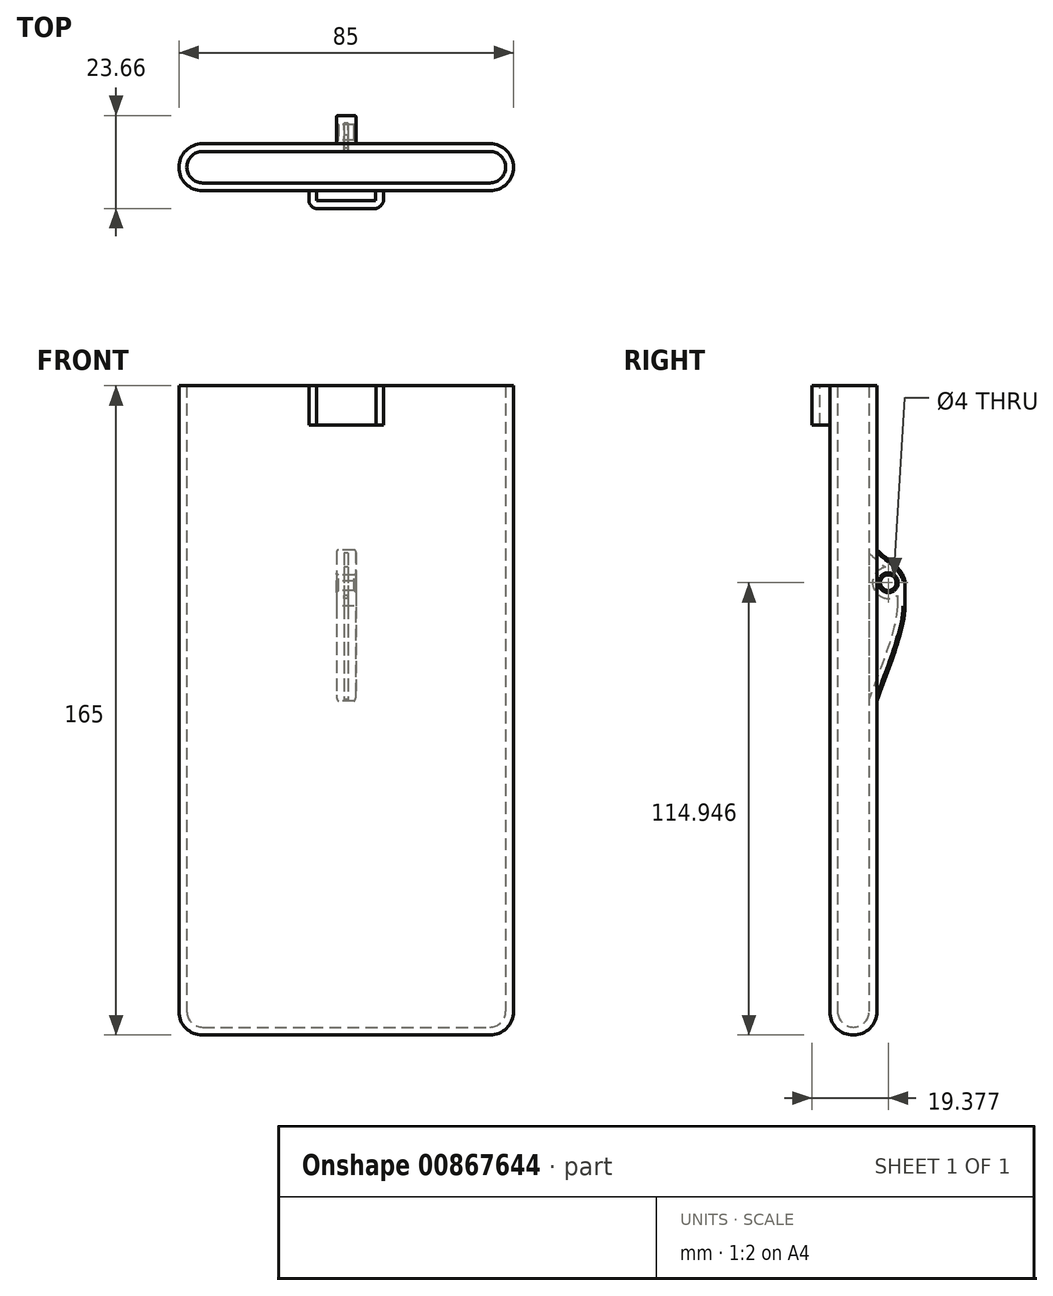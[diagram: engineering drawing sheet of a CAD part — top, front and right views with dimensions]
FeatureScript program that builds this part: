
annotation { "Feature Type Name" : "Feature", "Feature Type Description" : "" }
export const myFeature = defineFeature(function(context is Context, id is Id, definition is map)
    precondition{}
    {
        {
            var Q0;
            Q0=qCreatedBy(makeId("Front.planeOp"),FACE);
            var sketch = newSketch(context, id + "F0", { "sketchPlane" : qUnion([Q0])});
            skLineSegment(sketch, "E0.bottom", {"start": v(42.5, 82.5) * mm, "end": v(-42.5, 82.5) * mm});
            skLineSegment(sketch, "E0.top", {"start": v(36.5, -82.5) * mm, "end": v(-36.5, -82.5) * mm});
            skLineSegment(sketch, "E0.left", {"start": v(42.5, 82.5) * mm, "end": v(42.5, -76.5) * mm});
            skLineSegment(sketch, "E0.right", {"start": v(-42.5, 82.5) * mm, "end": v(-42.5, -76.5) * mm});
            skPoint(sketch, "E0.middle", {"position": v(0, 0) * mm});
            skPoint(sketch, "E1.orphan", {"position": v(-42.5, -82.5) * mm});
            skPoint(sketch, "E2.orphan", {"position": v(42.5, -82.5) * mm});
            skLineSegment(sketch, "E3", {"start": v(36.5, -82.5) * mm, "end": v(36.5, 82.5) * mm});
            skLineSegment(sketch, "E4", {"start": v(42.5, -76.5) * mm, "end": v(-42.5, -76.5) * mm});
            skLineSegment(sketch, "E5", {"start": v(-36.5, -82.5) * mm, "end": v(-36.5, 82.5) * mm});
            skArc(sketch, "E6", {"start": v(36.5, -82.5) * mm, "mid": v(40.74, -80.74) * mm, "end": v(42.5, -76.5) * mm});
            skArc(sketch, "E7", {"start": v(-42.5, -76.5) * mm, "mid": v(-40.74, -80.74) * mm, "end": v(-36.5, -82.5) * mm});
            skSolve(sketch);
        }
        {
            var Q0;
            Q0=qCreatedBy(makeId("Right.planeOp"),FACE);
            var sketch = newSketch(context, id + "F1", { "sketchPlane" : qUnion([Q0])});
            skLineSegment(sketch, "E8", {"start": v(20.64, 40.42) * mm, "end": v(20.69, 40.42) * mm});
            skLineSegment(sketch, "E9", {"start": v(13.16, 32.9) * mm, "end": v(13.16, 26.53) * mm});
            skFitSpline(sketch, "E10", {"points": [v(13.16, 26.53) * mm, v(5.97, 2.35) * mm], "startDerivative": vector(0.3, -17.47) * mm, "endDerivative": vector(-6.38, -18.09) * mm});
            skPoint(sketch, "E11.centerSnap0", {"position": v(16.3, 40.42) * mm});
            skArc(sketch, "E12", {"start": v(13.16, 32) * mm, "mid": v(13.2, 32.45) * mm, "end": v(13.16, 32.9) * mm});
            skPoint(sketch, "E13.orphan", {"position": v(13.16, 40.42) * mm});
            skLineSegment(sketch, "E14", {"start": v(6, 2.42) * mm, "end": v(5.97, 2.35) * mm});
            skFitSpline(sketch, "E15", {"points": [v(6, 40.79) * mm, v(13.16, 32.9) * mm], "startDerivative": vector(7.97, -7.88) * mm, "endDerivative": vector(2.73, -10.61) * mm});
            skPoint(sketch, "E16.end.orphan", {"position": v(19.43, 40.42) * mm});
            skLineSegment(sketch, "E17", {"start": v(6, 40.79) * mm, "end": v(6, 2.42) * mm});
            skCircle(sketch, "E18", {"center": v(8.88, 32.45) * mm, "radius": 2 * mm});
            skSolve(sketch);
        }
        {
            var Q0;
            {var subQ0=sQuery(id+"F0.wireOp",EDGE,"E3");var subQ1=sQuery(id+"F0.wireOp",EDGE,"E0.bottom");var subQ2=makeQuery(id+"F0.imprint","INTERSECT",VERTEX,{"derivedFrom":[subQ1,subQ0]});Q0=makeQuery(id+"F0.imprint","IMPRINT",FACE,{"disambiguationData":[TD([[makeQuery(id+"F0.imprint","IMPRINT",EDGE,{"disambiguationData":[TD([[subQ2,-1.0]])],"derivedFrom":subQ1}),1.0]])]});}
            extrude(context, id + "F2", {"entities" : qUnion([Q0]), "endBound" : BoundingType.SYMMETRIC, "depth" : 12 * mm, "offsetDistance" : 25 * mm});
        }
        {
            var Q0;
            {var subQ0=sQuery(id+"F0.wireOp",EDGE,"E0.right");Q0=makeQuery(id+"F0.imprint","IMPRINT",FACE,{"disambiguationData":[TD([[makeQuery(id+"F0.imprint","IMPRINT",EDGE,{"derivedFrom":subQ0}),1.0]])]});}
            var Q1;
            Q1=sQuery(id+"F0.wireOp",EDGE,"E5");
            revolve(context, id + "F3", {"operationType" : NewBodyOperationType.ADD, "surfaceOperationType" : NewSurfaceOperationType.NEW, "entities" : qUnion([Q0]), "axis" : qUnion([Q1]), "revolveType" : RevolveType.FULL});
        }
        {
            var Q0;
            {var subQ0=sQuery(id+"F0.wireOp",EDGE,"E0.left");Q0=makeQuery(id+"F0.imprint","IMPRINT",FACE,{"disambiguationData":[TD([[makeQuery(id+"F0.imprint","IMPRINT",EDGE,{"derivedFrom":subQ0}),-1.0]])]});}
            var Q1;
            Q1=sQuery(id+"F0.wireOp",EDGE,"E3");
            revolve(context, id + "F4", {"operationType" : NewBodyOperationType.ADD, "surfaceOperationType" : NewSurfaceOperationType.NEW, "entities" : qUnion([Q0]), "axis" : qUnion([Q1]), "revolveType" : RevolveType.FULL});
        }
        {
            var Q0;
            {var subQ0=sQuery(id+"F0.wireOp",EDGE,"E0.top");Q0=makeQuery(id+"F0.imprint","IMPRINT",FACE,{"disambiguationData":[TD([[makeQuery(id+"F0.imprint","IMPRINT",EDGE,{"derivedFrom":subQ0}),-1.0]])]});}
            var Q1;
            Q1=sQuery(id+"F0.wireOp",EDGE,"E4");
            revolve(context, id + "F5", {"operationType" : NewBodyOperationType.ADD, "surfaceOperationType" : NewSurfaceOperationType.NEW, "entities" : qUnion([Q0]), "axis" : qUnion([Q1]), "revolveType" : RevolveType.FULL});
        }
        {
            var Q0;
            {var subQ0=sQuery(id+"F0.wireOp",EDGE,"E6");Q0=makeQuery(id+"F0.imprint","IMPRINT",FACE,{"disambiguationData":[TD([[makeQuery(id+"F0.imprint","IMPRINT",EDGE,{"derivedFrom":subQ0}),1.0]])]});}
            var Q1;
            Q1=sQuery(id+"F0.wireOp",EDGE,"E4");
            revolve(context, id + "F6", {"operationType" : NewBodyOperationType.ADD, "surfaceOperationType" : NewSurfaceOperationType.NEW, "entities" : qUnion([Q0]), "axis" : qUnion([Q1]), "revolveType" : RevolveType.FULL});
        }
        {
            var Q0;
            {var subQ0=sQuery(id+"F0.wireOp",EDGE,"E7");Q0=makeQuery(id+"F0.imprint","IMPRINT",FACE,{"disambiguationData":[TD([[makeQuery(id+"F0.imprint","IMPRINT",EDGE,{"derivedFrom":subQ0}),1.0]])]});}
            var Q1;
            Q1=sQuery(id+"F0.wireOp",EDGE,"E4");
            revolve(context, id + "F7", {"operationType" : NewBodyOperationType.ADD, "surfaceOperationType" : NewSurfaceOperationType.NEW, "entities" : qUnion([Q0]), "axis" : qUnion([Q1]), "revolveType" : RevolveType.FULL});
        }
        {
            var Q0;
            {var subQ0=sQuery(id+"F1.wireOp",EDGE,"E10");Q0=makeQuery(id+"F1.imprint","IMPRINT",FACE,{"disambiguationData":[TD([[makeQuery(id+"F1.imprint","IMPRINT",EDGE,{"derivedFrom":subQ0}),-1.0]])]});}
            extrude(context, id + "F8", {"entities" : qUnion([Q0]), "operationType" : NewBodyOperationType.ADD, "endBound" : BoundingType.SYMMETRIC, "depth" : 5 * mm, "offsetDistance" : 25 * mm});
        }
        {
            var Q0;
            {var subQ0=sQuery(id+"F0.wireOp",EDGE,"E0.bottom");Q0=makeQuery(id+"F4.boolean.opBoolean","MERGE",FACE,{"derivedFrom":[makeQuery(id+"F3.boolean.opBoolean","MERGE",FACE,{"derivedFrom":[makeQuery(id+"F2.opExtrude","SWEPT_FACE",FACE,{"disambiguationData":[OSD([subQ0])]}),makeQuery(id+"F3.opRevolve","SWEPT_FACE",FACE,{"disambiguationData":[OSD([subQ0])]})]}),makeQuery(id+"F4.opRevolve","SWEPT_FACE",FACE,{"disambiguationData":[OSD([subQ0])]})]});}
            shell(context, id + "F9", {"entities" : qUnion([Q0]), "thickness" : 2 * mm});
        }
        {
            var Q0;
            Q0=makeQuery(id+"F8.opExtrude","CAP_EDGE",EDGE,{"disambiguationData":[OSD([sQuery(id+"F1.wireOp",EDGE,"E15")])],"isStart":false});
            var Q1;
            Q1=makeQuery(id+"F8.opExtrude","CAP_EDGE",EDGE,{"disambiguationData":[OSD([sQuery(id+"F1.wireOp",EDGE,"E9")])],"isStart":false});
            var Q2;
            Q2=makeQuery(id+"F8.opExtrude","CAP_EDGE",EDGE,{"disambiguationData":[OSD([sQuery(id+"F1.wireOp",EDGE,"E10")])],"isStart":false});
            var Q3;
            Q3=makeQuery(id+"F8.opExtrude","CAP_EDGE",EDGE,{"disambiguationData":[OSD([sQuery(id+"F1.wireOp",EDGE,"E10")])],"isStart":true});
            var Q4;
            Q4=makeQuery(id+"F8.opExtrude","CAP_EDGE",EDGE,{"disambiguationData":[OSD([sQuery(id+"F1.wireOp",EDGE,"E9")])],"isStart":true});
            var Q5;
            Q5=makeQuery(id+"F8.opExtrude","CAP_EDGE",EDGE,{"disambiguationData":[OSD([sQuery(id+"F1.wireOp",EDGE,"E15")])],"isStart":true});
            fillet(context, id + "F10", {"entities" : qUnion([Q0, Q1, Q2, Q3, Q4, Q5]), "radius" : 0.5 * mm, "tangentPropagation" : true, "allowEdgeOverflow" : false});
        }
        {
            var Q0;
            Q0=makeQuery(id+"F8.opExtrude","CAP_EDGE",EDGE,{"disambiguationData":[OSD([sQuery(id+"F1.wireOp",EDGE,"E18")])],"isStart":false});
            var Q1;
            Q1=makeQuery(id+"F8.opExtrude","CAP_EDGE",EDGE,{"disambiguationData":[OSD([sQuery(id+"F1.wireOp",EDGE,"E18")])],"isStart":true});
            chamfer(context, id + "F11", {"entities" : qUnion([Q0, Q1]), "width" : 0.5 * mm, "tangentPropagation" : true});
        }
        {
            var Q0;
            {var subQ0=sQuery(id+"F0.wireOp",EDGE,"E0.bottom");Q0=makeQuery(id+"F4.boolean.opBoolean","MERGE",FACE,{"derivedFrom":[makeQuery(id+"F3.boolean.opBoolean","MERGE",FACE,{"derivedFrom":[makeQuery(id+"F2.opExtrude","SWEPT_FACE",FACE,{"disambiguationData":[OSD([subQ0])]}),makeQuery(id+"F3.opRevolve","SWEPT_FACE",FACE,{"disambiguationData":[OSD([subQ0])]})]}),makeQuery(id+"F4.opRevolve","SWEPT_FACE",FACE,{"disambiguationData":[OSD([subQ0])]})]});}
            var sketch = newSketch(context, id + "F12", { "sketchPlane" : qUnion([Q0])});
            skSolve(sketch);
        }
        {
            var Q0;
            {var subQ1=sQuery(id+"F0.wireOp",EDGE,"E0.bottom");var subQ4=makeQuery(id+"F2.opExtrude","CAP_EDGE",EDGE,{"disambiguationData":[OSD([subQ1])],"isStart":true});Q0=makeQuery(id+"F12.imprint","IMPRINT",FACE,{"disambiguationData":[TD([[makeQuery(id+"F12.imprint","IMPRINT",EDGE,{"derivedFrom":subQ4}),1.0]])]});}
            var sketch = newSketch(context, id + "F13", { "sketchPlane" : qUnion([Q0])});
            skLineSegment(sketch, "E19.bottom", {"start": v(7.5, -8.5) * mm, "end": v(-7.5, -8.5) * mm});
            skLineSegment(sketch, "E19.top", {"start": v(7.5, -6) * mm, "end": v(-7.5, -6) * mm});
            skLineSegment(sketch, "E19.left", {"start": v(7.5, -8.5) * mm, "end": v(7.5, -6) * mm});
            skLineSegment(sketch, "E19.right", {"start": v(-7.5, -8.5) * mm, "end": v(-7.5, -6) * mm});
            skPoint(sketch, "E19.middle", {"position": v(0, -7.25) * mm});
            skLineSegment(sketch, "E20.0", {"start": v(7.52, -10.5) * mm, "end": v(-7.5, -10.5) * mm});
            skLineSegment(sketch, "E21.0", {"start": v(9.5, -8.5) * mm, "end": v(9.5, -6) * mm});
            skLineSegment(sketch, "E22.0", {"start": v(-9.5, -8.5) * mm, "end": v(-9.5, -6) * mm});
            skFitSpline(sketch, "E23", {"points": [v(9.5, -8.5) * mm, v(7.52, -10.5) * mm], "startDerivative": vector(0, -1.6) * mm, "endDerivative": vector(-2.74, -0.18) * mm});
            skFitSpline(sketch, "E24", {"points": [v(-7.5, -10.5) * mm, v(-9.5, -8.5) * mm], "startDerivative": vector(-3.19, 0.1) * mm, "endDerivative": vector(-0.1, 2.71) * mm});
            skLineSegment(sketch, "E25", {"start": v(-10.23, -8.5) * mm, "end": v(10.6, -8.5) * mm, "construction": true});
            skSolve(sketch);
        }
        {
            var Q0;
            {var subQ1=sQuery(id+"F13.wireOp",EDGE,"E19.bottom");Q0=makeQuery(id+"F13.imprint","IMPRINT",FACE,{"disambiguationData":[TD([[makeQuery(id+"F13.imprint","IMPRINT",EDGE,{"derivedFrom":subQ1}),1.0]])]});}
            extrude(context, id + "F14", {"entities" : qUnion([Q0]), "oppositeDirection" : true, "depth" : 10 * mm, "offsetDistance" : 25 * mm});
        }
    });
